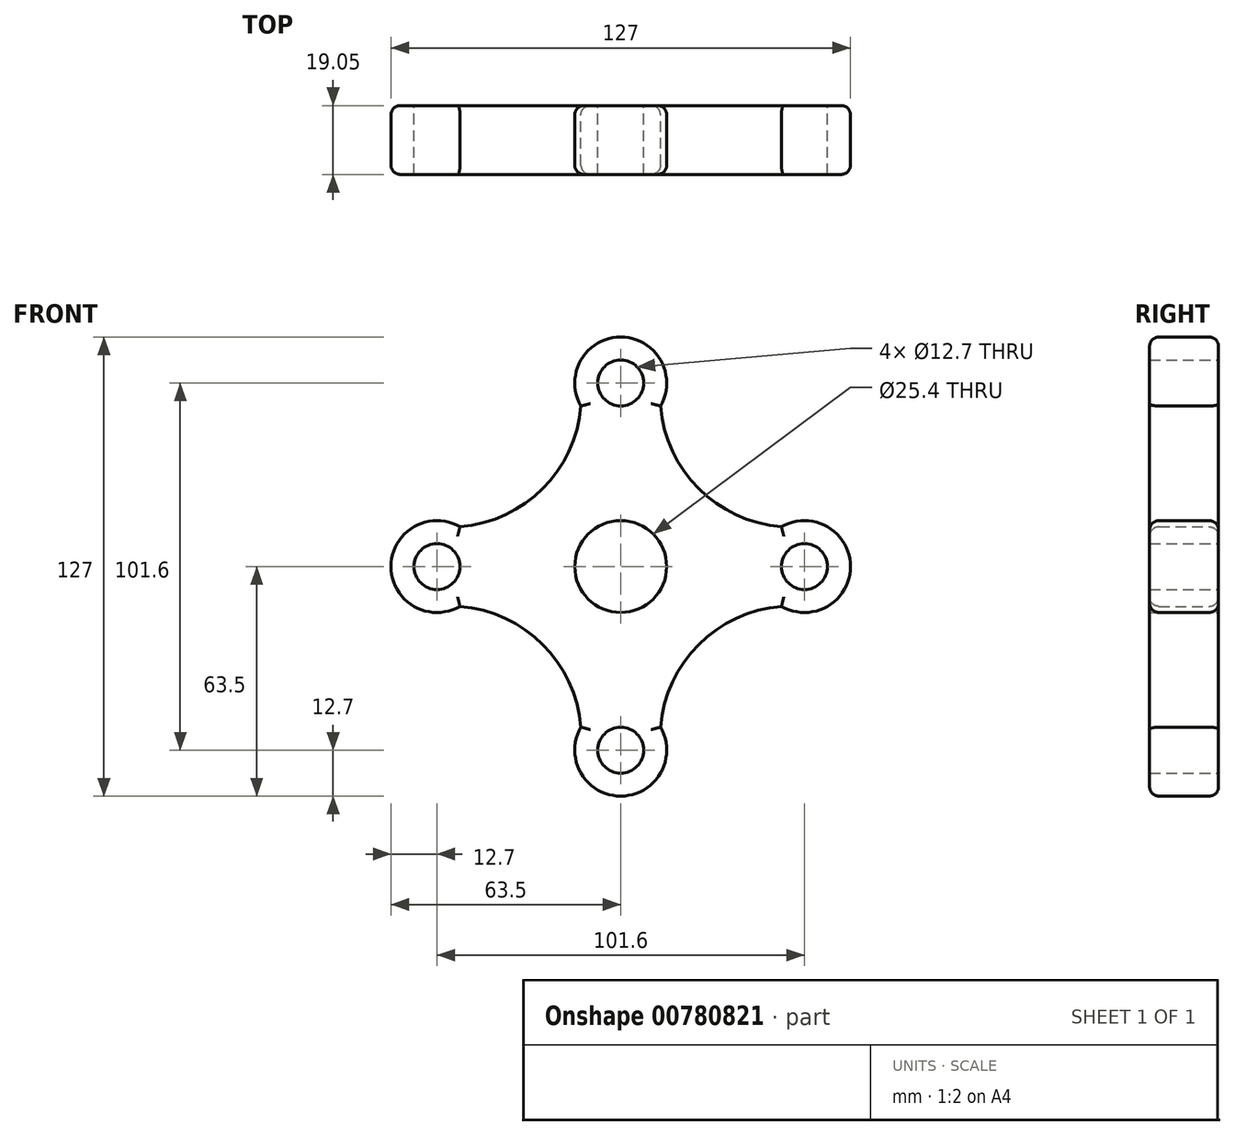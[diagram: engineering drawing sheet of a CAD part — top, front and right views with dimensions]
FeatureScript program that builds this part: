
annotation { "Feature Type Name" : "Feature", "Feature Type Description" : "" }
export const myFeature = defineFeature(function(context is Context, id is Id, definition is map)
    precondition{}
    {
        {
            var Q0;
            Q0=qCreatedBy(makeId("Front.planeOp"),FACE);
            var sketch = newSketch(context, id + "F0", { "sketchPlane" : qUnion([Q0])});
            skCircle(sketch, "E0", {"center": v(0, 0) * mm, "radius": 12.7 * mm});
            skCircle(sketch, "E1", {"center": v(0, 50.8) * mm, "radius": 6.35 * mm});
            skCircle(sketch, "E2", {"center": v(-50.8, 0) * mm, "radius": 6.35 * mm});
            skCircle(sketch, "E3", {"center": v(0, -50.8) * mm, "radius": 6.35 * mm});
            skCircle(sketch, "E4", {"center": v(50.8, 0) * mm, "radius": 6.35 * mm});
            skArc(sketch, "E5", {"start": v(11, 44.45) * mm, "mid": v(0, 63.5) * mm, "end": v(-11, 44.45) * mm});
            skArc(sketch, "E6", {"start": v(-44.45, 11) * mm, "mid": v(-63.5, 0) * mm, "end": v(-44.45, -11) * mm});
            skArc(sketch, "E7", {"start": v(-11, -44.45) * mm, "mid": v(0, -63.5) * mm, "end": v(11, -44.45) * mm});
            skArc(sketch, "E8", {"start": v(44.45, -11) * mm, "mid": v(63.5, 0) * mm, "end": v(44.45, 11) * mm});
            skArc(sketch, "E9", {"start": v(11, 44.45) * mm, "mid": v(21.57, 21.57) * mm, "end": v(44.45, 11) * mm});
            skArc(sketch, "E10", {"start": v(-44.45, 11) * mm, "mid": v(-21.57, 21.57) * mm, "end": v(-11, 44.45) * mm});
            skArc(sketch, "E11", {"start": v(-11, -44.45) * mm, "mid": v(-21.57, -21.57) * mm, "end": v(-44.45, -11) * mm});
            skArc(sketch, "E12", {"start": v(44.45, -11) * mm, "mid": v(21.57, -21.57) * mm, "end": v(11, -44.45) * mm});
            skPoint(sketch, "E13.trimOffspring.end.orphan", {"position": v(73.23, 0) * mm});
            skSolve(sketch);
        }
        {
            var Q0;
            Q0=makeQuery(id+"F0.imprint","IMPRINT",FACE,{"disambiguationData":[TD([[makeQuery(id+"F0.imprint","IMPRINT",EDGE,{"derivedFrom":sQuery(id+"F0.wireOp",EDGE,"E0")}),-1.0]])]});
            extrude(context, id + "F1", {"entities" : qUnion([Q0]), "depth" : 19.05 * mm, "offsetDistance" : 25.4 * mm});
        }
        {
            var Q0;
            Q0=makeQuery(id+"F1.opExtrude","CAP_EDGE",EDGE,{"disambiguationData":[OSD([sQuery(id+"F0.wireOp",EDGE,"E10")])],"isStart":false});
            var Q1;
            Q1=makeQuery(id+"F1.opExtrude","CAP_EDGE",EDGE,{"disambiguationData":[OSD([sQuery(id+"F0.wireOp",EDGE,"E5")])],"isStart":false});
            var Q2;
            Q2=makeQuery(id+"F1.opExtrude","CAP_EDGE",EDGE,{"disambiguationData":[OSD([sQuery(id+"F0.wireOp",EDGE,"E9")])],"isStart":false});
            var Q3;
            Q3=makeQuery(id+"F1.opExtrude","CAP_EDGE",EDGE,{"disambiguationData":[OSD([sQuery(id+"F0.wireOp",EDGE,"E8")])],"isStart":false});
            var Q4;
            Q4=makeQuery(id+"F1.opExtrude","CAP_EDGE",EDGE,{"disambiguationData":[OSD([sQuery(id+"F0.wireOp",EDGE,"E12")])],"isStart":false});
            var Q5;
            Q5=makeQuery(id+"F1.opExtrude","CAP_EDGE",EDGE,{"disambiguationData":[OSD([sQuery(id+"F0.wireOp",EDGE,"E7")])],"isStart":false});
            var Q6;
            Q6=makeQuery(id+"F1.opExtrude","CAP_EDGE",EDGE,{"disambiguationData":[OSD([sQuery(id+"F0.wireOp",EDGE,"E11")])],"isStart":false});
            var Q7;
            Q7=makeQuery(id+"F1.opExtrude","CAP_EDGE",EDGE,{"disambiguationData":[OSD([sQuery(id+"F0.wireOp",EDGE,"E6")])],"isStart":false});
            var Q8;
            Q8=makeQuery(id+"F1.opExtrude","CAP_EDGE",EDGE,{"disambiguationData":[OSD([sQuery(id+"F0.wireOp",EDGE,"E9")])],"isStart":true});
            var Q9;
            Q9=makeQuery(id+"F1.opExtrude","CAP_EDGE",EDGE,{"disambiguationData":[OSD([sQuery(id+"F0.wireOp",EDGE,"E5")])],"isStart":true});
            var Q10;
            Q10=makeQuery(id+"F1.opExtrude","CAP_EDGE",EDGE,{"disambiguationData":[OSD([sQuery(id+"F0.wireOp",EDGE,"E10")])],"isStart":true});
            var Q11;
            Q11=makeQuery(id+"F1.opExtrude","CAP_EDGE",EDGE,{"disambiguationData":[OSD([sQuery(id+"F0.wireOp",EDGE,"E6")])],"isStart":true});
            var Q12;
            Q12=makeQuery(id+"F1.opExtrude","CAP_EDGE",EDGE,{"disambiguationData":[OSD([sQuery(id+"F0.wireOp",EDGE,"E11")])],"isStart":true});
            var Q13;
            Q13=makeQuery(id+"F1.opExtrude","CAP_EDGE",EDGE,{"disambiguationData":[OSD([sQuery(id+"F0.wireOp",EDGE,"E7")])],"isStart":true});
            var Q14;
            Q14=makeQuery(id+"F1.opExtrude","CAP_EDGE",EDGE,{"disambiguationData":[OSD([sQuery(id+"F0.wireOp",EDGE,"E12")])],"isStart":true});
            var Q15;
            Q15=makeQuery(id+"F1.opExtrude","CAP_EDGE",EDGE,{"disambiguationData":[OSD([sQuery(id+"F0.wireOp",EDGE,"E8")])],"isStart":true});
            fillet(context, id + "F2", {"entities" : qUnion([Q0, Q1, Q2, Q3, Q4, Q5, Q6, Q7, Q8, Q9, Q10, Q11, Q12, Q13, Q14, Q15]), "radius" : 2.54 * mm, "tangentPropagation" : true, "allowEdgeOverflow" : false});
        }
    });
